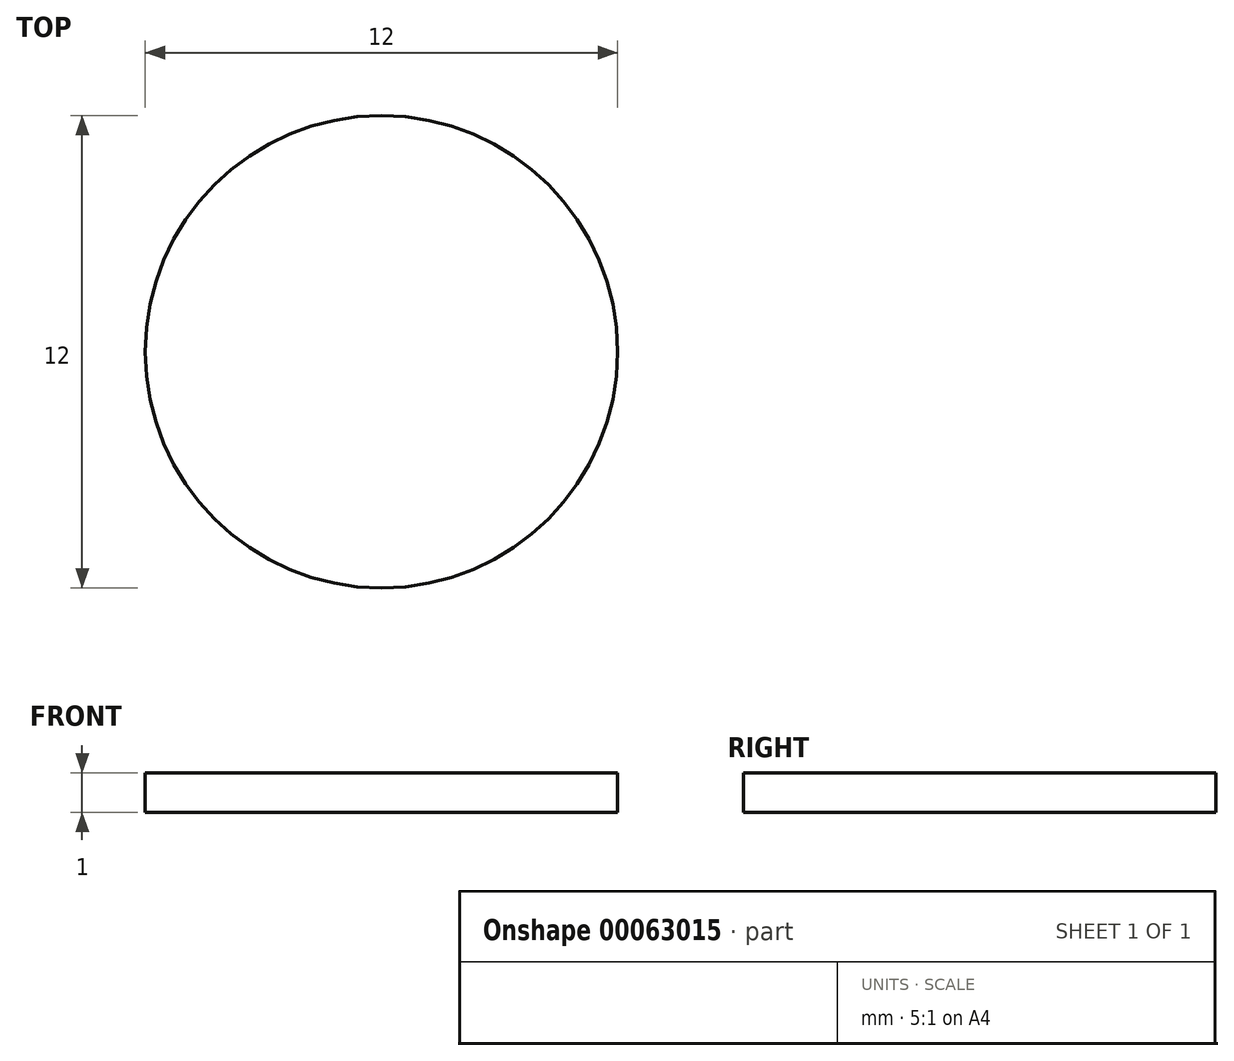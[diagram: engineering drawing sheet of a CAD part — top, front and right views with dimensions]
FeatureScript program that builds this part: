
annotation { "Feature Type Name" : "Feature", "Feature Type Description" : "" }
export const myFeature = defineFeature(function(context is Context, id is Id, definition is map)
    precondition{}
    {
        {
            var Q0;
            Q0=qCreatedBy(makeId("Top.planeOp"),FACE);
            var sketch = newSketch(context, id + "F0", { "sketchPlane" : qUnion([Q0])});
            skCircle(sketch, "E0", {"center": v(0, 0) * mm, "radius": 6 * mm});
            skSolve(sketch);
        }
        {
            var Q0;
            Q0=makeQuery(id+"F0.imprint","IMPRINT",FACE,{"disambiguationData":[TD([[makeQuery(id+"F0.imprint","IMPRINT",EDGE,{"derivedFrom":sQuery(id+"F0.wireOp",EDGE,"E0")}),1.0]])]});
            extrude(context, id + "F1", {"entities" : qUnion([Q0]), "depth" : 1 * mm});
        }
    });
